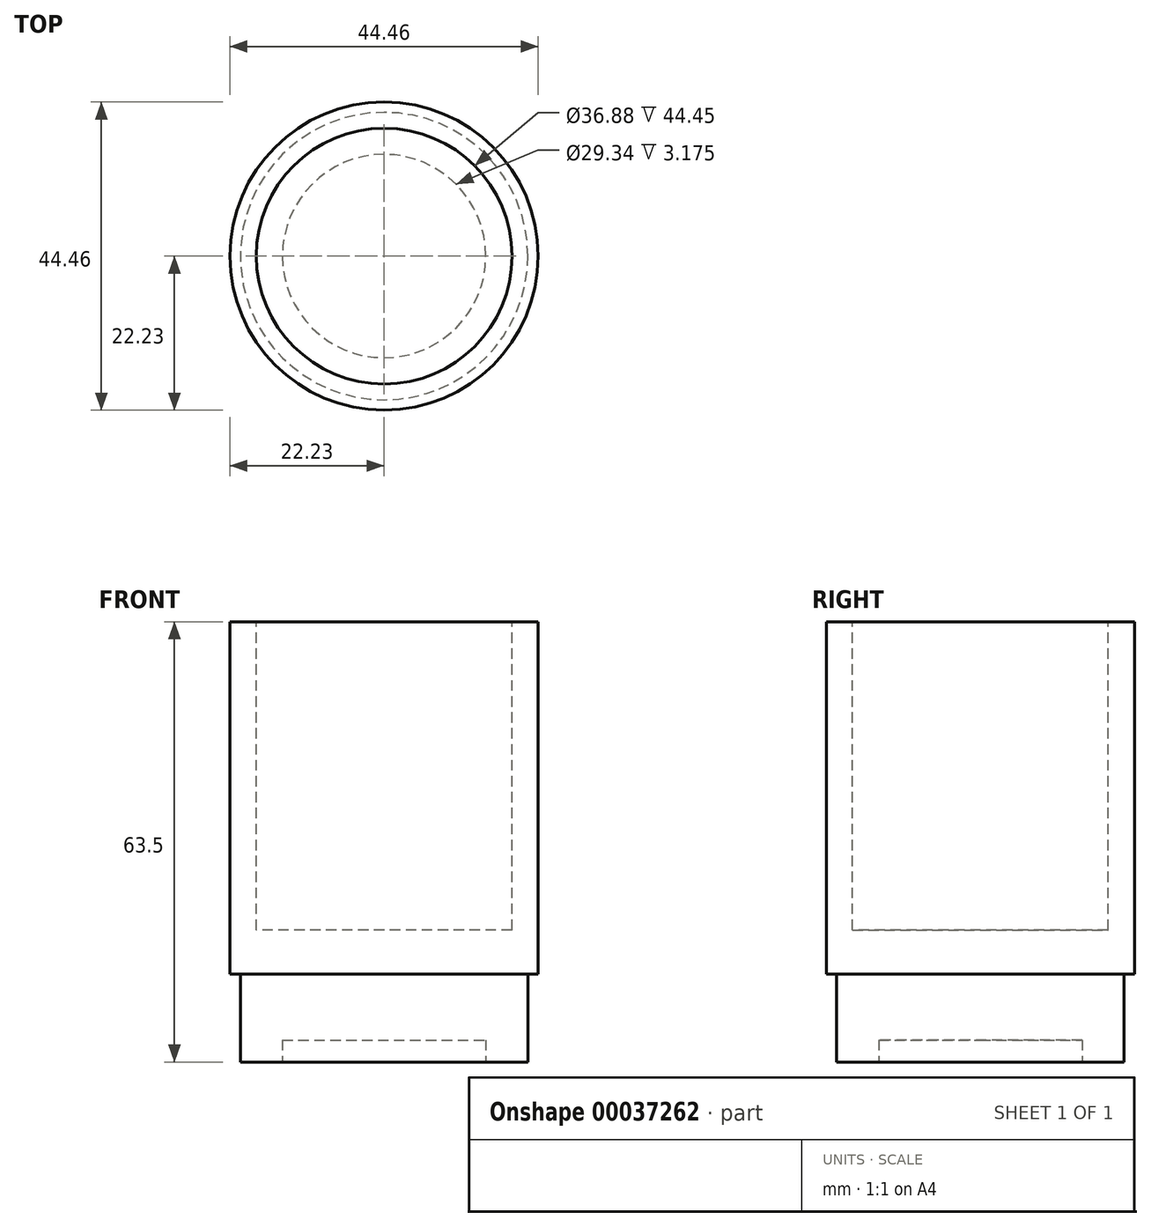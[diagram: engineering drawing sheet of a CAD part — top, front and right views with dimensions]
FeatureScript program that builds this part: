
annotation { "Feature Type Name" : "Feature", "Feature Type Description" : "" }
export const myFeature = defineFeature(function(context is Context, id is Id, definition is map)
    precondition{}
    {
        {
            var Q0;
            Q0=qCreatedBy(makeId("Top.planeOp"),FACE);
            var sketch = newSketch(context, id + "F0", { "sketchPlane" : qUnion([Q0])});
            skCircle(sketch, "E0", {"center": v(0, 0) * mm, "radius": 22.23 * mm});
            skSolve(sketch);
        }
        {
            var Q0;
            Q0=makeQuery(id+"F0.imprint","IMPRINT",FACE,{"disambiguationData":[TD([[makeQuery(id+"F0.imprint","IMPRINT",EDGE,{"derivedFrom":sQuery(id+"F0.wireOp",EDGE,"E0")}),1.0]])]});
            extrude(context, id + "F1", {"entities" : qUnion([Q0]), "depth" : 63.5 * mm});
        }
        {
            var Q0;
            Q0=makeQuery(id+"F1.opExtrude","CAP_FACE",FACE,{"disambiguationData":[OSD([sQuery(id+"F0.wireOp",EDGE,"E0")])],"isStart":false});
            var sketch = newSketch(context, id + "F2", { "sketchPlane" : qUnion([Q0])});
            skCircle(sketch, "E1", {"center": v(0, 0) * mm, "radius": 18.44 * mm});
            skSolve(sketch);
        }
        {
            var Q0;
            Q0 = qSketchRegion(id + "F2", true);
            extrude(context, id + "F3", {"entities" : qUnion([Q0]), "operationType" : NewBodyOperationType.REMOVE, "oppositeDirection" : true, "depth" : 44.45 * mm});
        }
        {
            var Q0;
            Q0=makeQuery(id+"F1.opExtrude","CAP_FACE",FACE,{"disambiguationData":[OSD([sQuery(id+"F0.wireOp",EDGE,"E0")])],"isStart":true});
            var sketch = newSketch(context, id + "F4", { "sketchPlane" : qUnion([Q0])});
            skCircle(sketch, "E2", {"center": v(0, 0) * mm, "radius": 20.73 * mm});
            skSolve(sketch);
        }
        {
            var Q0;
            Q0=makeQuery(id+"F4.imprint","IMPRINT",FACE,{"disambiguationData":[TD([[makeQuery(id+"F4.imprint","IMPRINT",EDGE,{"derivedFrom":sQuery(id+"F4.wireOp",EDGE,"E2")}),-1.0]])]});
            extrude(context, id + "F5", {"entities" : qUnion([Q0]), "operationType" : NewBodyOperationType.REMOVE, "oppositeDirection" : true, "depth" : 12.7 * mm});
        }
        {
            var Q0;
            Q0=makeQuery(id+"F1.opExtrude","CAP_FACE",FACE,{"disambiguationData":[OSD([sQuery(id+"F0.wireOp",EDGE,"E0")])],"isStart":true});
            var sketch = newSketch(context, id + "F6", { "sketchPlane" : qUnion([Q0])});
            skCircle(sketch, "E3", {"center": v(0, 0) * mm, "radius": 14.67 * mm});
            skSolve(sketch);
        }
        {
            var Q0;
            Q0=makeQuery(id+"F6.imprint","IMPRINT",FACE,{"disambiguationData":[TD([[makeQuery(id+"F6.imprint","IMPRINT",EDGE,{"derivedFrom":sQuery(id+"F6.wireOp",EDGE,"E3")}),1.0]])]});
            var Q1;
            Q1=makeQuery(id+"F1.opExtrude","CAP_FACE",FACE,{"disambiguationData":[OSD([sQuery(id+"F0.wireOp",EDGE,"E0")])],"isStart":false});
            extrude(context, id + "F7", {"entities" : qUnion([Q0, Q1]), "operationType" : NewBodyOperationType.REMOVE, "oppositeDirection" : true, "depth" : 3.17 * mm});
        }
    });
